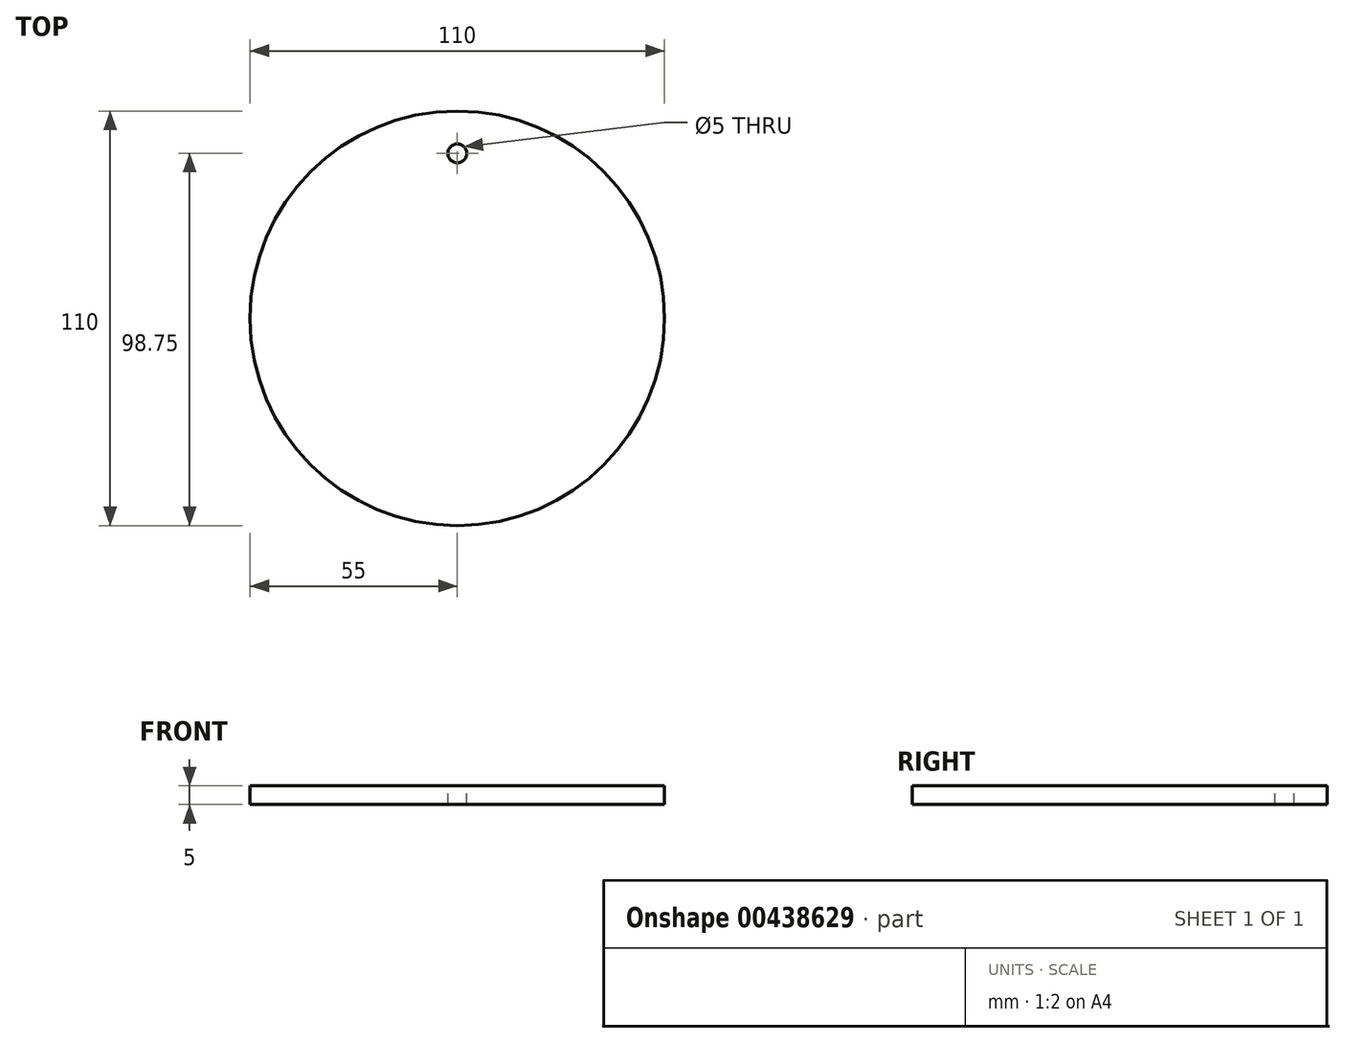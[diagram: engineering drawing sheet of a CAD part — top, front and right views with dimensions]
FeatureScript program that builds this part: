
annotation { "Feature Type Name" : "Feature", "Feature Type Description" : "" }
export const myFeature = defineFeature(function(context is Context, id is Id, definition is map)
    precondition{}
    {
        {
            var Q0;
            Q0=qCreatedBy(makeId("Top.planeOp"),FACE);
            var sketch = newSketch(context, id + "F0", { "sketchPlane" : qUnion([Q0])});
            skCircle(sketch, "E0", {"center": v(0, 0) * mm, "radius": 55 * mm});
            skSolve(sketch);
        }
        {
            var Q0;
            Q0=makeQuery(id+"F0.imprint","IMPRINT",FACE,{"disambiguationData":[TD([[makeQuery(id+"F0.imprint","IMPRINT",EDGE,{"derivedFrom":sQuery(id+"F0.wireOp",EDGE,"E0")}),1.0]])]});
            extrude(context, id + "F1", {"entities" : qUnion([Q0]), "depth" : 5 * mm});
        }
        {
            var Q0;
            Q0=makeQuery(id+"F1.opExtrude","CAP_FACE",FACE,{"disambiguationData":[OSD([sQuery(id+"F0.wireOp",EDGE,"E0")])],"isStart":false});
            var sketch = newSketch(context, id + "F2", { "sketchPlane" : qUnion([Q0])});
            skCircle(sketch, "E1", {"center": v(0, 43.75) * mm, "radius": 2.5 * mm});
            skSolve(sketch);
        }
        {
            var Q0;
            Q0 = qSketchRegion(id + "F2", true);
            extrude(context, id + "F3", {"entities" : qUnion([Q0]), "operationType" : NewBodyOperationType.REMOVE, "endBound" : BoundingType.THROUGH_ALL, "oppositeDirection" : true, "depth" : 25 * mm});
        }
        {
            var Q0;
            Q0=qCreatedBy(makeId("Right.planeOp"),FACE);
            var sketch = newSketch(context, id + "F4", { "sketchPlane" : qUnion([Q0])});
            skLineSegment(sketch, "E2", {"start": v(0, 0) * mm, "end": v(0, 28.43) * mm});
            skSolve(sketch);
        }
    });
